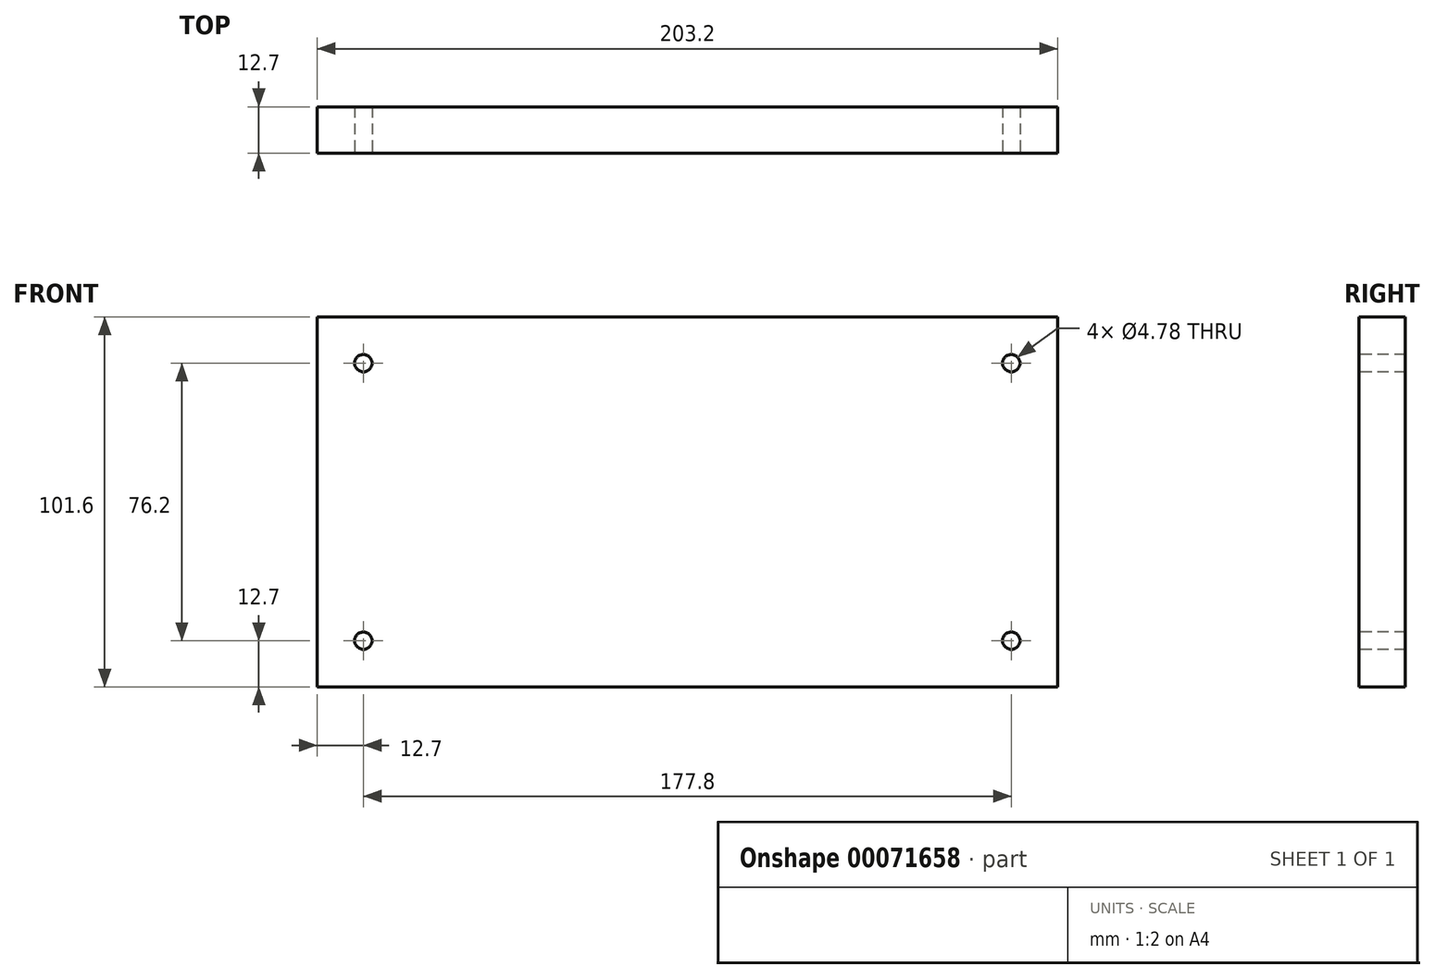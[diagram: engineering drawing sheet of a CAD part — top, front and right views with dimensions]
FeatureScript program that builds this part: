
annotation { "Feature Type Name" : "Feature", "Feature Type Description" : "" }
export const myFeature = defineFeature(function(context is Context, id is Id, definition is map)
    precondition{}
    {
        {
            var Q0;
            Q0=qCreatedBy(makeId("Front.planeOp"),FACE);
            var sketch = newSketch(context, id + "F0", { "sketchPlane" : qUnion([Q0])});
            skLineSegment(sketch, "E0.bottom", {"start": v(0, 0) * mm, "end": v(203.2, 0) * mm});
            skLineSegment(sketch, "E0.top", {"start": v(0, 101.6) * mm, "end": v(203.2, 101.6) * mm});
            skLineSegment(sketch, "E0.left", {"start": v(0, 0) * mm, "end": v(0, 101.6) * mm});
            skLineSegment(sketch, "E0.right", {"start": v(203.2, 0) * mm, "end": v(203.2, 101.6) * mm});
            skSolve(sketch);
        }
        {
            var Q0;
            Q0 = qSketchRegion(id + "F0", true);
            extrude(context, id + "F1", {"entities" : qUnion([Q0]), "depth" : 12.7 * mm});
        }
        {
            var Q0;
            Q0=makeQuery(id+"F1.opExtrude","CAP_FACE",FACE,{"disambiguationData":[OSD([sQuery(id+"F0.wireOp",EDGE,"E0.bottom"),sQuery(id+"F0.wireOp",EDGE,"E0.top"),sQuery(id+"F0.wireOp",EDGE,"E0.left"),sQuery(id+"F0.wireOp",EDGE,"E0.right")])],"isStart":false});
            var sketch = newSketch(context, id + "F2", { "sketchPlane" : qUnion([Q0])});
            skPoint(sketch, "E1", {"position": v(12.7, 12.7) * mm});
            skPoint(sketch, "E2", {"position": v(190.5, 12.7) * mm});
            skPoint(sketch, "E3", {"position": v(12.7, 88.9) * mm});
            skPoint(sketch, "E4", {"position": v(190.5, 88.9) * mm});
            skSolve(sketch);
        }
        {
            var Q0;
            Q0=sQuery(id+"F2.wireOp",VERTEX,"E1");
            var Q1;
            Q1=sQuery(id+"F2.wireOp",VERTEX,"E2");
            var Q2;
            Q2=sQuery(id+"F2.wireOp",VERTEX,"E4");
            var Q3;
            Q3=sQuery(id+"F2.wireOp",VERTEX,"E3");
            var Q4;
            Q4=makeQuery(id+"F1.opExtrude","SWEPT_BODY",BODY,{"disambiguationData":[OSD([sQuery(id+"F0.wireOp",EDGE,"E0.bottom"),sQuery(id+"F0.wireOp",EDGE,"E0.top"),sQuery(id+"F0.wireOp",EDGE,"E0.left"),sQuery(id+"F0.wireOp",EDGE,"E0.right")])]});
            hole(context, id + "F3", {"style" : HoleStyle.SIMPLE, "endStyle" : HoleEndStyle.THROUGH, "holeDiameter" : 4.78 * mm, "locations" : qUnion([Q0, Q1, Q2, Q3]), "scope" : qUnion([Q4]), "isTappedThrough" : true});
        }
    });
